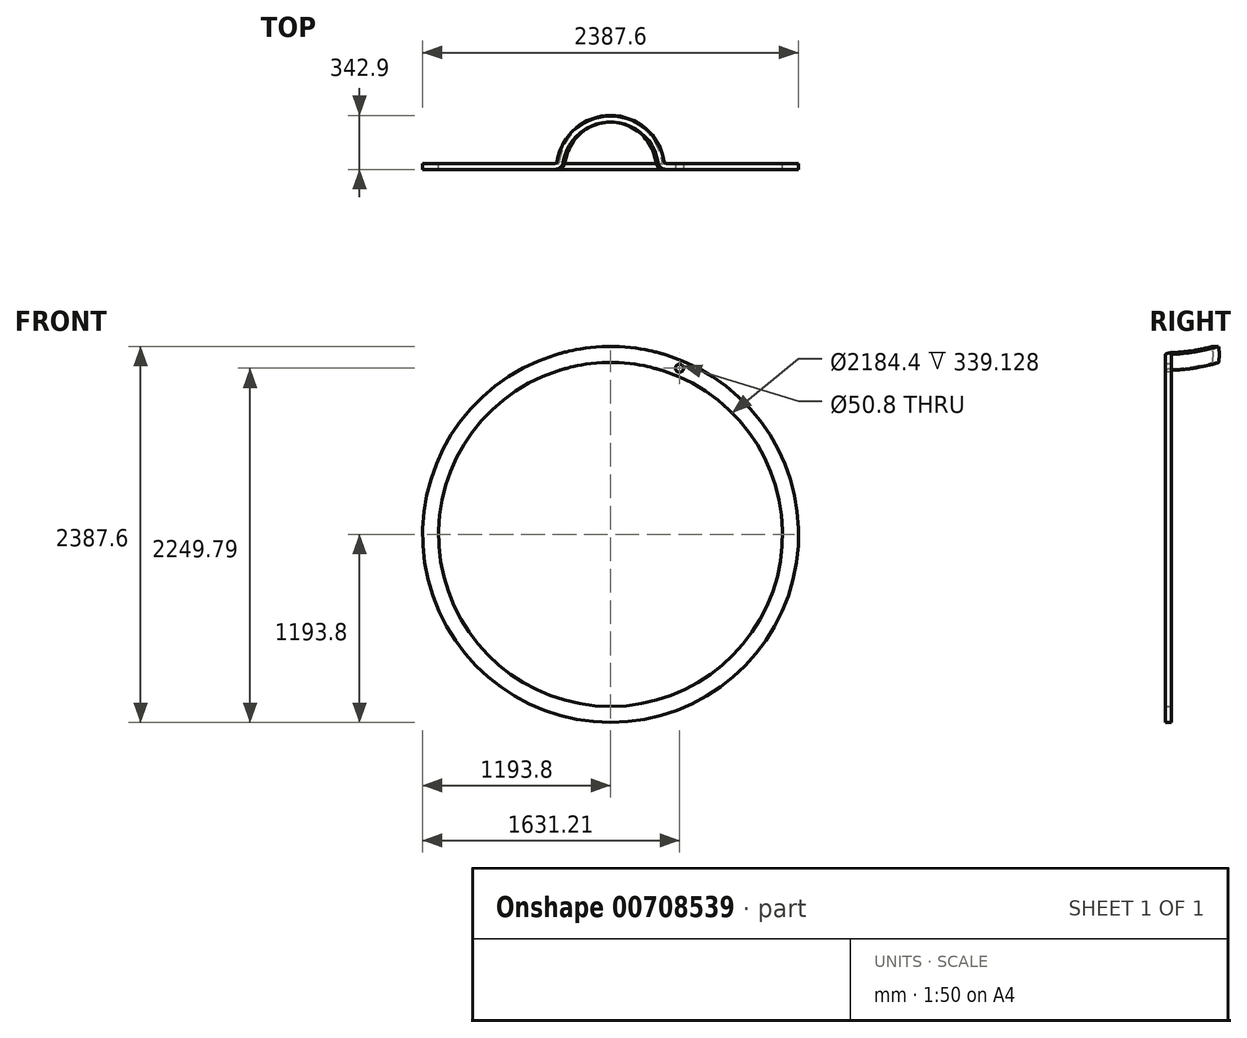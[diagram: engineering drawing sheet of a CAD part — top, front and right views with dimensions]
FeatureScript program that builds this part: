
annotation { "Feature Type Name" : "Feature", "Feature Type Description" : "" }
export const myFeature = defineFeature(function(context is Context, id is Id, definition is map)
    precondition{}
    {
        {
            var Q0;
            Q0=qCreatedBy(makeId("Front.planeOp"),FACE);
            var sketch = newSketch(context, id + "F0", { "sketchPlane" : qUnion([Q0])});
            skCircle(sketch, "E0", {"center": v(0, 0) * mm, "radius": 1092.2 * mm});
            skCircle(sketch, "E1", {"center": v(0, 0) * mm, "radius": 1193.8 * mm});
            skSolve(sketch);
        }
        {
            var Q0;
            Q0 = qSketchRegion(id + "F0", true);
            extrude(context, id + "F1", {"entities" : qUnion([Q0]), "depth" : 406.4 * mm, "offsetDistance" : 25.4 * mm});
        }
        {
            var Q0;
            Q0=makeQuery(id+"F1.opExtrude","CAP_FACE",FACE,{"disambiguationData":[OSD([sQuery(id+"F0.wireOp",EDGE,"E0"),sQuery(id+"F0.wireOp",EDGE,"E1")])],"isStart":false});
            var sketch = newSketch(context, id + "F2", { "sketchPlane" : qUnion([Q0])});
            skLineSegment(sketch, "E2", {"start": v(0, 0) * mm, "end": v(0, 1447.8) * mm});
            skLineSegment(sketch, "E3", {"start": v(0, 1447.8) * mm, "end": v(0, 838.2) * mm});
            skArc(sketch, "E4", {"start": v(0, 1447.8) * mm, "mid": v(304.8, 1143) * mm, "end": v(0, 838.2) * mm});
            skSolve(sketch);
        }
        {
            var Q0;
            Q0 = qSketchRegion(id + "F2", true);
            var Q1;
            Q1=sQuery(id+"F2.wireOp",EDGE,"E3");
            revolve(context, id + "F3", {"operationType" : NewBodyOperationType.REMOVE, "surfaceOperationType" : NewSurfaceOperationType.NEW, "entities" : qUnion([Q0]), "axis" : qUnion([Q1]), "revolveType" : RevolveType.FULL, "oppositeDirection" : true});
        }
        {
            var Q0;
            Q0=makeQuery(id+"F3.boolean.opBoolean","INTERSECT",EDGE,{"disambiguationData":[OD(0.0)],"derivedFrom":[makeQuery(id+"F1.opExtrude","CAP_FACE",FACE,{"disambiguationData":[OSD([sQuery(id+"F0.wireOp",EDGE,"E0"),sQuery(id+"F0.wireOp",EDGE,"E1")])],"isStart":false}),makeQuery(id+"F3.opRevolve","SWEPT_FACE",FACE,{"disambiguationData":[OSD([sQuery(id+"F2.wireOp",EDGE,"E4")])]})]});
            var Q1;
            Q1=makeQuery(id+"F3.boolean.opBoolean","INTERSECT",EDGE,{"disambiguationData":[OD(1.0)],"derivedFrom":[makeQuery(id+"F1.opExtrude","CAP_FACE",FACE,{"disambiguationData":[OSD([sQuery(id+"F0.wireOp",EDGE,"E0"),sQuery(id+"F0.wireOp",EDGE,"E1")])],"isStart":false}),makeQuery(id+"F3.opRevolve","SWEPT_FACE",FACE,{"disambiguationData":[OSD([sQuery(id+"F2.wireOp",EDGE,"E4")])]})]});
            fillet(context, id + "F4", {"entities" : qUnion([Q0, Q1]), "radius" : 53.34 * mm, "tangentPropagation" : true, "allowEdgeOverflow" : false});
        }
        {
            var Q0;
            Q0=qCreatedBy(makeId("Top.planeOp"),FACE);
            var sketch = newSketch(context, id + "F5", { "sketchPlane" : qUnion([Q0])});
            skLineSegment(sketch, "E5", {"start": v(0, 0) * mm, "end": v(0, -1171.83) * mm});
            skSolve(sketch);
        }
        {
            var Q0;
            Q0=makeQuery(id+"F1.opExtrude","SWEPT_FACE",FACE,{"disambiguationData":[OSD([sQuery(id+"F0.wireOp",EDGE,"E1")])]});
            var Q1;
            Q1=makeQuery(id+"F1.opExtrude","CAP_FACE",FACE,{"disambiguationData":[OSD([sQuery(id+"F0.wireOp",EDGE,"E0"),sQuery(id+"F0.wireOp",EDGE,"E1")])],"isStart":true});
            var Q2;
            Q2=makeQuery(id+"F1.opExtrude","SWEPT_FACE",FACE,{"disambiguationData":[OSD([sQuery(id+"F0.wireOp",EDGE,"E0")])]});
            shell(context, id + "F6", {"entities" : qUnion([Q0, Q1, Q2]), "thickness" : 38.1 * mm});
        }
        {
            var Q0;
            {var subQ0=sQuery(id+"F0.wireOp",EDGE,"E0");var subQ2=sQuery(id+"F0.wireOp",EDGE,"E1");var subQ4=sQuery(id+"F2.wireOp",EDGE,"E4");var subQ5=makeQuery(id+"F1.opExtrude","CAP_FACE",FACE,{"disambiguationData":[OSD([subQ0,subQ2])],"isStart":false});var subQ6=makeQuery(id+"F4.opFillet","BLEND_FACE",FACE,{"disambiguationData":[OSD([subQ0,subQ2,subQ4]),TDD([makeQuery(id+"F3.boolean.opBoolean","INTERSECT",EDGE,{"disambiguationData":[OD(1.0)],"derivedFrom":[subQ5,makeQuery(id+"F3.opRevolve","SWEPT_FACE",FACE,{"disambiguationData":[OSD([subQ4])]})]})])]});Q0=makeQuery(id+"Fyoqt6IOsad0GUR_1.7.F3.boolean.opBoolean","SPLIT",FACE,{"disambiguationData":[TD([subQ6])],"derivedFrom":makeQuery(id+"Fyoqt6IOsad0GUR_1.6.F3.boolean.opBoolean","SPLIT",FACE,{"disambiguationData":[TD([subQ6])],"derivedFrom":makeQuery(id+"Fyoqt6IOsad0GUR_1.5.F3.boolean.opBoolean","SPLIT",FACE,{"disambiguationData":[TD([subQ6])],"derivedFrom":makeQuery(id+"Fyoqt6IOsad0GUR_1.4.F3.boolean.opBoolean","SPLIT",FACE,{"disambiguationData":[TD([subQ6])],"derivedFrom":makeQuery(id+"Fyoqt6IOsad0GUR_1.3.F3.boolean.opBoolean","SPLIT",FACE,{"disambiguationData":[TD([subQ6])],"derivedFrom":makeQuery(id+"Fyoqt6IOsad0GUR_1.2.F3.boolean.opBoolean","SPLIT",FACE,{"disambiguationData":[TD([subQ6])],"derivedFrom":makeQuery(id+"Fyoqt6IOsad0GUR_1.1.F3.boolean.opBoolean","SPLIT",FACE,{"disambiguationData":[TD([subQ6])],"derivedFrom":subQ5})})})})})})});}
            var sketch = newSketch(context, id + "F7", { "sketchPlane" : qUnion([Q0])});
            skCircle(sketch, "E6", {"center": v(437.4, 1056) * mm, "radius": 25.4 * mm});
            skSolve(sketch);
        }
        {
            var Q0;
            Q0=makeQuery(id+"F7.imprint","IMPRINT",FACE,{"disambiguationData":[TD([[makeQuery(id+"F7.imprint","IMPRINT",EDGE,{"derivedFrom":sQuery(id+"F7.wireOp",EDGE,"E6")}),1.0]])]});
            var Q1;
            Q1=sQuery(id+"F7.wireOp",EDGE,"E6");
            extrude(context, id + "F8", {"entities" : qUnion([Q0]), "operationType" : NewBodyOperationType.REMOVE, "surfaceEntities" : qUnion([Q1]), "endBound" : BoundingType.THROUGH_ALL, "oppositeDirection" : true, "depth" : 25.4 * mm, "offsetDistance" : 25.4 * mm});
        }
        {
            var Q0;
            Q0=qCreatedBy(makeId("Top.planeOp"),FACE);
            var sketch = newSketch(context, id + "F9", { "sketchPlane" : qUnion([Q0])});
            skLineSegment(sketch, "E7", {"start": v(0, 0) * mm, "end": v(0, -928.4) * mm});
            skSolve(sketch);
        }
    });
